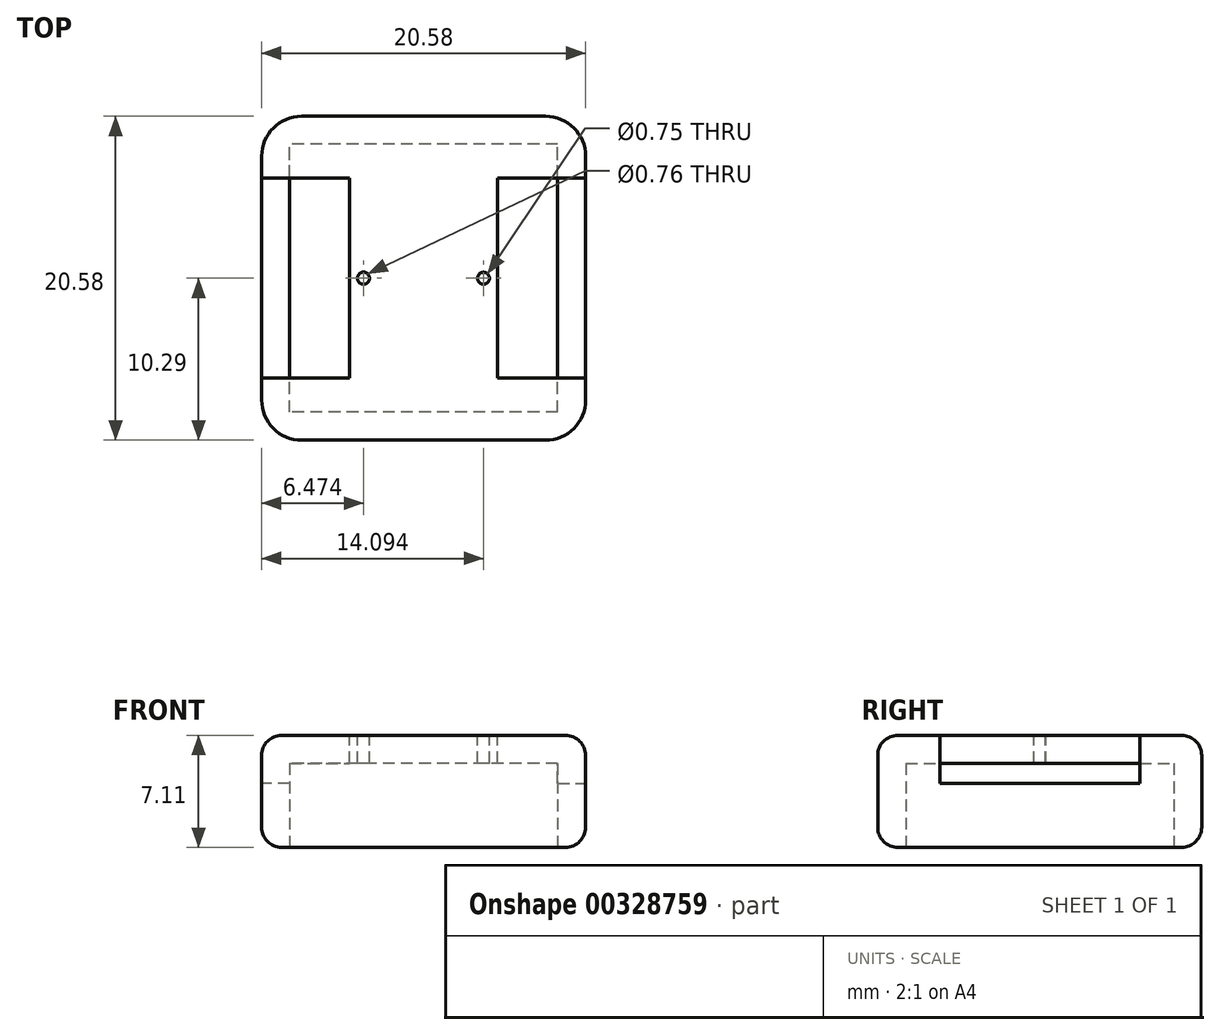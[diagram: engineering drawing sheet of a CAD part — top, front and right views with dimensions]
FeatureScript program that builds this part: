
annotation { "Feature Type Name" : "Feature", "Feature Type Description" : "" }
export const myFeature = defineFeature(function(context is Context, id is Id, definition is map)
    precondition{}
    {
        {
            var Q0;
            Q0=qCreatedBy(makeId("Top.planeOp"),FACE);
            var sketch = newSketch(context, id + "F0", { "sketchPlane" : qUnion([Q0])});
            skLineSegment(sketch, "E0.bottom", {"start": v(10.29, 10.29) * mm, "end": v(-10.29, 10.29) * mm});
            skLineSegment(sketch, "E0.top", {"start": v(10.29, -10.29) * mm, "end": v(-10.29, -10.29) * mm});
            skLineSegment(sketch, "E0.left", {"start": v(10.29, 10.29) * mm, "end": v(10.29, -10.29) * mm});
            skLineSegment(sketch, "E0.right", {"start": v(-10.29, 10.29) * mm, "end": v(-10.29, -10.29) * mm});
            skPoint(sketch, "E0.middle", {"position": v(0, 0) * mm});
            skSolve(sketch);
        }
        {
            var Q0;
            Q0=qSketchRegion(id+"F0",true);
            extrude(context, id + "F1", {"entities" : qUnion([Q0]), "depth" : 7.11 * mm});
        }
        {
            var Q0;
            Q0=makeQuery(id+"F1.opExtrude","CAP_FACE",FACE,{"disambiguationData":[OSD([sQuery(id+"F0.wireOp",EDGE,"E0.bottom"),sQuery(id+"F0.wireOp",EDGE,"E0.top"),sQuery(id+"F0.wireOp",EDGE,"E0.left"),sQuery(id+"F0.wireOp",EDGE,"E0.right")])],"isStart":true});
            var sketch = newSketch(context, id + "F2", { "sketchPlane" : qUnion([Q0])});
            skLineSegment(sketch, "E1.bottom", {"start": v(8.5, 8.5) * mm, "end": v(-8.5, 8.5) * mm});
            skLineSegment(sketch, "E1.top", {"start": v(8.5, -8.5) * mm, "end": v(-8.5, -8.5) * mm});
            skLineSegment(sketch, "E1.left", {"start": v(8.5, 8.5) * mm, "end": v(8.5, -8.5) * mm});
            skLineSegment(sketch, "E1.right", {"start": v(-8.5, 8.5) * mm, "end": v(-8.5, -8.5) * mm});
            skPoint(sketch, "E1.middle", {"position": v(0, 0) * mm});
            skSolve(sketch);
        }
        {
            var Q0;
            Q0=makeQuery(id+"F2.imprint","IMPRINT",FACE,{"disambiguationData":[TD([[makeQuery(id+"F2.imprint","IMPRINT",EDGE,{"derivedFrom":sQuery(id+"F2.wireOp",EDGE,"E1.bottom")}),1.0]])]});
            extrude(context, id + "F3", {"entities" : qUnion([Q0]), "operationType" : NewBodyOperationType.REMOVE, "oppositeDirection" : true, "depth" : 5.33 * mm});
        }
        {
            var Q0;
            Q0=makeQuery(id+"F1.opExtrude","SWEPT_EDGE",EDGE,{"disambiguationData":[OSD([sQuery(id+"F0.wireOp",EDGE,"E0.top"),sQuery(id+"F0.wireOp",EDGE,"E0.right")])]});
            var Q1;
            Q1=makeQuery(id+"F1.opExtrude","SWEPT_EDGE",EDGE,{"disambiguationData":[OSD([sQuery(id+"F0.wireOp",EDGE,"E0.bottom"),sQuery(id+"F0.wireOp",EDGE,"E0.left")])]});
            var Q2;
            Q2=makeQuery(id+"F1.opExtrude","SWEPT_EDGE",EDGE,{"disambiguationData":[OSD([sQuery(id+"F0.wireOp",EDGE,"E0.top"),sQuery(id+"F0.wireOp",EDGE,"E0.left")])]});
            var Q3;
            Q3=makeQuery(id+"F1.opExtrude","SWEPT_EDGE",EDGE,{"disambiguationData":[OSD([sQuery(id+"F0.wireOp",EDGE,"E0.bottom"),sQuery(id+"F0.wireOp",EDGE,"E0.right")])]});
            fillet(context, id + "F4", {"entities" : qUnion([Q0, Q1, Q2, Q3]), "radius" : 2.54 * mm, "tangentPropagation" : true, "allowEdgeOverflow" : false});
        }
        {
            var Q0;
            Q0=makeQuery(id+"F1.opExtrude","CAP_FACE",FACE,{"disambiguationData":[OSD([sQuery(id+"F0.wireOp",EDGE,"E0.bottom"),sQuery(id+"F0.wireOp",EDGE,"E0.top"),sQuery(id+"F0.wireOp",EDGE,"E0.left"),sQuery(id+"F0.wireOp",EDGE,"E0.right")])],"isStart":false});
            var sketch = newSketch(context, id + "F5", { "sketchPlane" : qUnion([Q0])});
            skLineSegment(sketch, "E2.bottom", {"start": v(-4.7, 6.35) * mm, "end": v(-15.88, 6.35) * mm});
            skLineSegment(sketch, "E2.top", {"start": v(-4.7, -6.35) * mm, "end": v(-15.88, -6.35) * mm});
            skLineSegment(sketch, "E2.left", {"start": v(-4.7, 6.35) * mm, "end": v(-4.7, -6.35) * mm});
            skLineSegment(sketch, "E2.right", {"start": v(-15.88, 6.35) * mm, "end": v(-15.88, -6.35) * mm});
            skPoint(sketch, "E2.middle", {"position": v(-10.29, 0) * mm});
            skSolve(sketch);
        }
        {
            var Q0;
            {var subQ0=sQuery(id+"F5.wireOp",EDGE,"E2.left");Q0=makeQuery(id+"F5.imprint","IMPRINT",FACE,{"disambiguationData":[TD([[makeQuery(id+"F5.imprint","IMPRINT",EDGE,{"derivedFrom":subQ0}),-1.0]])]});}
            extrude(context, id + "F6", {"entities" : qUnion([Q0]), "operationType" : NewBodyOperationType.REMOVE, "oppositeDirection" : true, "depth" : 3.05 * mm});
        }
        {
            var Q0;
            Q0=makeQuery(id+"F1.opExtrude","CAP_FACE",FACE,{"disambiguationData":[OSD([sQuery(id+"F0.wireOp",EDGE,"E0.bottom"),sQuery(id+"F0.wireOp",EDGE,"E0.top"),sQuery(id+"F0.wireOp",EDGE,"E0.left"),sQuery(id+"F0.wireOp",EDGE,"E0.right")])],"isStart":false});
            var sketch = newSketch(context, id + "F7", { "sketchPlane" : qUnion([Q0])});
            skLineSegment(sketch, "E3.bottom", {"start": v(4.7, 6.35) * mm, "end": v(15.88, 6.35) * mm});
            skLineSegment(sketch, "E3.top", {"start": v(4.7, -6.35) * mm, "end": v(15.88, -6.35) * mm});
            skLineSegment(sketch, "E3.left", {"start": v(4.7, 6.35) * mm, "end": v(4.7, -6.35) * mm});
            skLineSegment(sketch, "E3.right", {"start": v(15.88, 6.35) * mm, "end": v(15.88, -6.35) * mm});
            skPoint(sketch, "E3.middle", {"position": v(10.29, 0) * mm});
            skSolve(sketch);
        }
        {
            var Q0;
            Q0=qSketchRegion(id+"F7",true);
            extrude(context, id + "F8", {"entities" : qUnion([Q0]), "operationType" : NewBodyOperationType.REMOVE, "oppositeDirection" : true, "depth" : 3.05 * mm});
        }
        {
            var Q0;
            Q0=makeQuery(id+"F1.opExtrude","CAP_FACE",FACE,{"disambiguationData":[OSD([sQuery(id+"F0.wireOp",EDGE,"E0.bottom"),sQuery(id+"F0.wireOp",EDGE,"E0.top"),sQuery(id+"F0.wireOp",EDGE,"E0.left"),sQuery(id+"F0.wireOp",EDGE,"E0.right")])],"isStart":false});
            var sketch = newSketch(context, id + "F9", { "sketchPlane" : qUnion([Q0])});
            skPoint(sketch, "E4.middle", {"position": v(0, 0) * mm});
            skCircle(sketch, "E5", {"center": v(-3.82, 0) * mm, "radius": 0.38 * mm});
            skCircle(sketch, "E6", {"center": v(3.8, 0) * mm, "radius": 0.38 * mm});
            skSolve(sketch);
        }
        {
            var Q0;
            Q0=qSketchRegion(id+"F9",true);
            extrude(context, id + "F10", {"entities" : qUnion([Q0]), "operationType" : NewBodyOperationType.REMOVE, "oppositeDirection" : true, "depth" : 1.78 * mm});
        }
        {
            var Q0;
            Q0=makeQuery(id+"F1.opExtrude","CAP_EDGE",EDGE,{"disambiguationData":[OSD([sQuery(id+"F0.wireOp",EDGE,"E0.bottom")])],"isStart":false});
            var Q1;
            Q1=makeQuery(id+"F1.opExtrude","CAP_EDGE",EDGE,{"disambiguationData":[OSD([sQuery(id+"F0.wireOp",EDGE,"E0.top")])],"isStart":false});
            fillet(context, id + "F11", {"entities" : qUnion([Q0, Q1]), "radius" : 1.27 * mm, "tangentPropagation" : true, "allowEdgeOverflow" : false});
        }
        {
            var Q0;
            Q0=makeQuery(id+"F1.opExtrude","CAP_EDGE",EDGE,{"disambiguationData":[OSD([sQuery(id+"F0.wireOp",EDGE,"E0.right")])],"isStart":true});
            var Q1;
            Q1=makeQuery(id+"F1.opExtrude","CAP_EDGE",EDGE,{"disambiguationData":[OSD([sQuery(id+"F0.wireOp",EDGE,"E0.bottom")])],"isStart":true});
            var Q2;
            {var subQ0=sQuery(id+"F0.wireOp",EDGE,"E0.right");var subQ1=sQuery(id+"F0.wireOp",EDGE,"E0.bottom");Q2=makeQuery(id+"F4.opFillet","BLEND_EDGE",EDGE,{"blendedFrom":[makeQuery(id+"F1.opExtrude","SWEPT_EDGE",EDGE,{"disambiguationData":[OSD([subQ1,subQ0])]}),makeQuery(id+"F1.opExtrude","CAP_FACE",FACE,{"disambiguationData":[OSD([subQ1,sQuery(id+"F0.wireOp",EDGE,"E0.top"),sQuery(id+"F0.wireOp",EDGE,"E0.left"),subQ0])],"isStart":true})],"blendedInto":[makeQuery(id+"F1.opExtrude","CAP_FACE",FACE,{"disambiguationData":[OSD([subQ1,sQuery(id+"F0.wireOp",EDGE,"E0.top"),sQuery(id+"F0.wireOp",EDGE,"E0.left"),subQ0])],"isStart":true})]});}
            fillet(context, id + "F12", {"entities" : qUnion([Q0, Q1, Q2]), "radius" : 1.27 * mm, "tangentPropagation" : true, "allowEdgeOverflow" : false});
        }
    });
